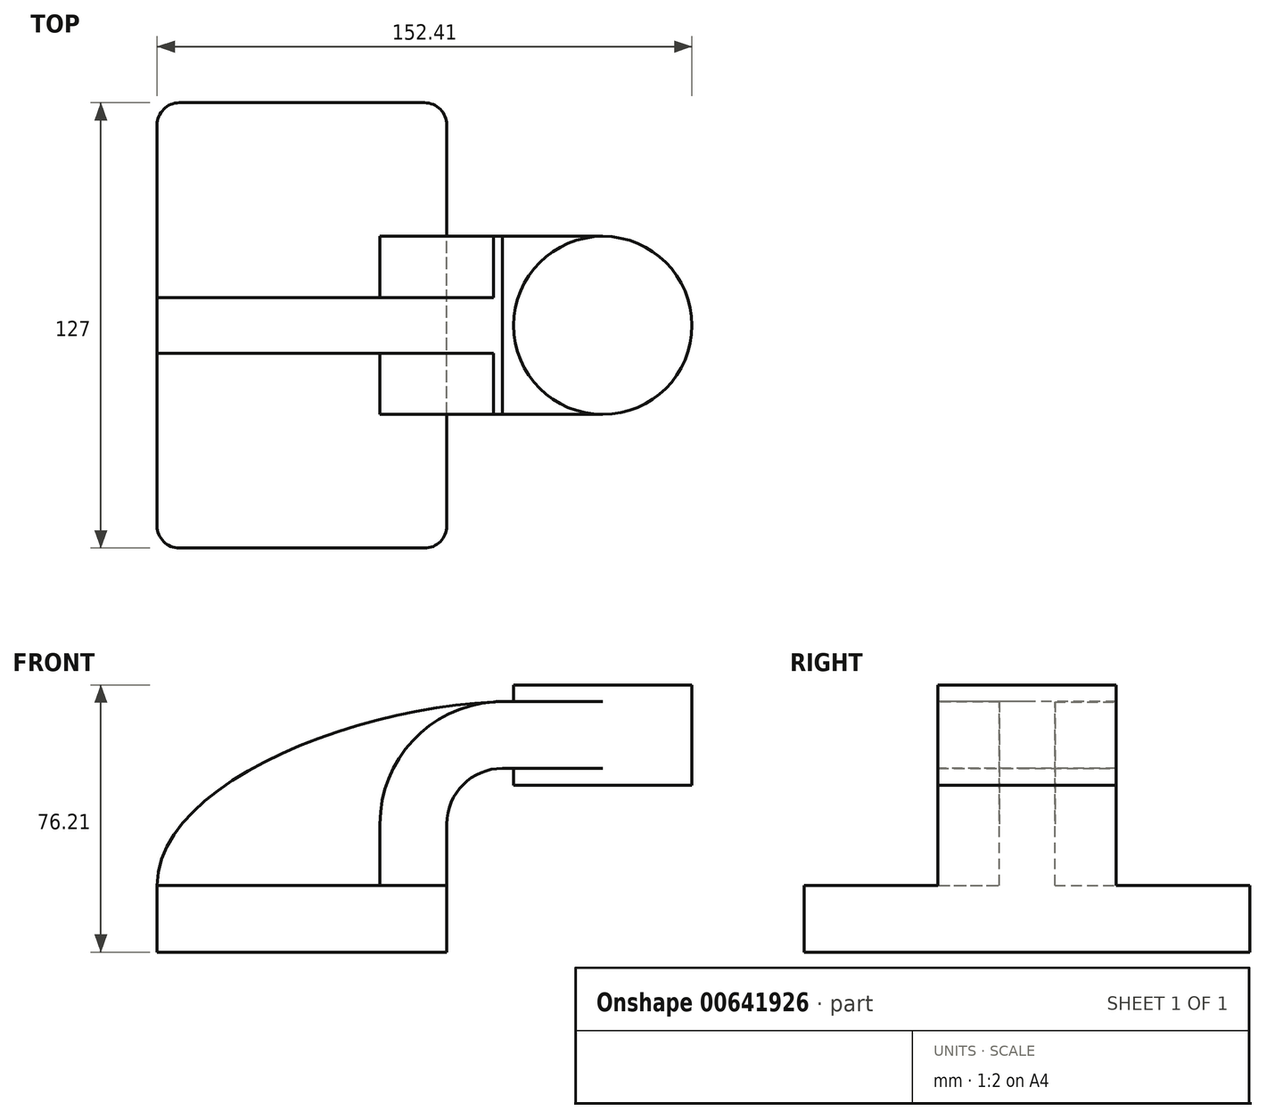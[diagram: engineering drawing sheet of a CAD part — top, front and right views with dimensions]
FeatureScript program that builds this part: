
annotation { "Feature Type Name" : "Feature", "Feature Type Description" : "" }
export const myFeature = defineFeature(function(context is Context, id is Id, definition is map)
    precondition{}
    {
        {
            var Q0;
            Q0=qCreatedBy(makeId("Front.planeOp"),FACE);
            var sketch = newSketch(context, id + "F0", { "sketchPlane" : qUnion([Q0])});
            skLineSegment(sketch, "E0.bottom", {"start": v(-41.28, 9.52) * mm, "end": v(41.28, 9.53) * mm});
            skLineSegment(sketch, "E0.top", {"start": v(-41.27, -9.52) * mm, "end": v(41.28, -9.52) * mm});
            skLineSegment(sketch, "E0.left", {"start": v(-41.27, 9.52) * mm, "end": v(-41.27, -9.53) * mm});
            skLineSegment(sketch, "E0.right", {"start": v(41.28, 9.52) * mm, "end": v(41.28, -9.52) * mm});
            skPoint(sketch, "E0.middle", {"position": v(0, 0) * mm});
            skLineSegment(sketch, "E1.bottom", {"start": v(60.32, 66.68) * mm, "end": v(111.12, 66.68) * mm});
            skLineSegment(sketch, "E1.top", {"start": v(60.32, 38.1) * mm, "end": v(111.12, 38.1) * mm});
            skLineSegment(sketch, "E1.left", {"start": v(60.32, 66.68) * mm, "end": v(60.32, 38.1) * mm});
            skLineSegment(sketch, "E1.right", {"start": v(111.12, 66.68) * mm, "end": v(111.12, 38.1) * mm});
            skPoint(sketch, "E1.middle", {"position": v(85.72, 52.39) * mm});
            skLineSegment(sketch, "E2", {"start": v(41.28, 9.52) * mm, "end": v(41.28, 27) * mm});
            skArc(sketch, "E3", {"start": v(41.28, 27) * mm, "mid": v(45.92, 38.23) * mm, "end": v(57.15, 42.88) * mm});
            skLineSegment(sketch, "E4", {"start": v(57.15, 42.88) * mm, "end": v(85.72, 42.88) * mm});
            skPoint(sketch, "E4.endSnap0", {"position": v(85.72, 38.1) * mm});
            skLineSegment(sketch, "E5.0", {"start": v(57.15, 61.93) * mm, "end": v(85.72, 61.93) * mm});
            skArc(sketch, "E5.1", {"start": v(22.23, 27) * mm, "mid": v(32.45, 51.7) * mm, "end": v(57.15, 61.93) * mm});
            skLineSegment(sketch, "E5.2", {"start": v(22.23, 9.52) * mm, "end": v(22.23, 27) * mm});
            skFitSpline(sketch, "E6", {"points": [v(-41.27, 9.52) * mm, v(57.15, 61.93) * mm], "startDerivative": vector(0.55, 89.13) * mm, "endDerivative": vector(120.23, 3.2) * mm});
            skLineSegment(sketch, "E7", {"start": v(85.72, 42.88) * mm, "end": v(85.72, 66.68) * mm});
            skLineSegment(sketch, "E8", {"start": v(85.72, 38.1) * mm, "end": v(85.72, 66.68) * mm});
            skSolve(sketch);
        }
        {
            var Q0;
            Q0=makeQuery(id+"F0.imprint","IMPRINT",FACE,{"disambiguationData":[TD([[makeQuery(id+"F0.imprint","IMPRINT",EDGE,{"derivedFrom":sQuery(id+"F0.wireOp",EDGE,"E0.top")}),1.0]])]});
            extrude(context, id + "F1", {"entities" : qUnion([Q0]), "endBound" : BoundingType.SYMMETRIC, "depth" : 127 * mm, "offsetDistance" : 25.4 * mm});
        }
        {
            var Q0;
            {var subQ1=sQuery(id+"F0.wireOp",EDGE,"E2");Q0=makeQuery(id+"F0.imprint","IMPRINT",FACE,{"disambiguationData":[TD([[makeQuery(id+"F0.imprint","IMPRINT",EDGE,{"derivedFrom":subQ1}),1.0]])]});}
            var Q1;
            {var subQ0=sQuery(id+"F0.wireOp",EDGE,"E5.0");var subQ1=sQuery(id+"F0.wireOp",EDGE,"E1.left");var subQ2=makeQuery(id+"F0.imprint","INTERSECT",VERTEX,{"derivedFrom":[subQ1,subQ0]});Q1=makeQuery(id+"F0.imprint","IMPRINT",FACE,{"disambiguationData":[TD([[makeQuery(id+"F0.imprint","IMPRINT",EDGE,{"disambiguationData":[TD([[subQ2,-1.0]])],"derivedFrom":subQ1}),1.0]])]});}
            extrude(context, id + "F2", {"entities" : qUnion([Q0, Q1]), "operationType" : NewBodyOperationType.ADD, "endBound" : BoundingType.SYMMETRIC, "depth" : 50.8 * mm, "offsetDistance" : 25.4 * mm});
        }
        {
            var Q0;
            {var subQ3=sQuery(id+"F0.wireOp",EDGE,"E5.2");Q0=makeQuery(id+"F0.imprint","IMPRINT",FACE,{"disambiguationData":[TD([[makeQuery(id+"F0.imprint","IMPRINT",EDGE,{"derivedFrom":subQ3}),1.0]])]});}
            extrude(context, id + "F3", {"entities" : qUnion([Q0]), "operationType" : NewBodyOperationType.ADD, "endBound" : BoundingType.SYMMETRIC, "depth" : 15.88 * mm, "offsetDistance" : 25.4 * mm});
        }
        {
            var Q0;
            {var subQ4=sQuery(id+"F0.wireOp",EDGE,"E1.right");Q0=makeQuery(id+"F0.imprint","IMPRINT",FACE,{"disambiguationData":[TD([[makeQuery(id+"F0.imprint","IMPRINT",EDGE,{"derivedFrom":subQ4}),-1.0]])]});}
            var Q1;
            Q1=sQuery(id+"F0.wireOp",EDGE,"E8");
            revolve(context, id + "F4", {"operationType" : NewBodyOperationType.ADD, "entities" : qUnion([Q0]), "axis" : qUnion([Q1]), "revolveType" : RevolveType.FULL});
        }
        {
            var Q0;
            Q0=makeQuery(id+"F1.opExtrude","CAP_EDGE",EDGE,{"disambiguationData":[OSD([sQuery(id+"F0.wireOp",EDGE,"E0.right")])],"isStart":false});
            var Q1;
            Q1=makeQuery(id+"F1.opExtrude","CAP_EDGE",EDGE,{"disambiguationData":[OSD([sQuery(id+"F0.wireOp",EDGE,"E0.left")])],"isStart":false});
            var Q2;
            Q2=makeQuery(id+"F1.opExtrude","CAP_EDGE",EDGE,{"disambiguationData":[OSD([sQuery(id+"F0.wireOp",EDGE,"E0.right")])],"isStart":true});
            var Q3;
            Q3=makeQuery(id+"F1.opExtrude","CAP_EDGE",EDGE,{"disambiguationData":[OSD([sQuery(id+"F0.wireOp",EDGE,"E0.left")])],"isStart":true});
            fillet(context, id + "F5", {"entities" : qUnion([Q0, Q1, Q2, Q3]), "radius" : 6.35 * mm, "tangentPropagation" : true, "allowEdgeOverflow" : false});
        }
    });
